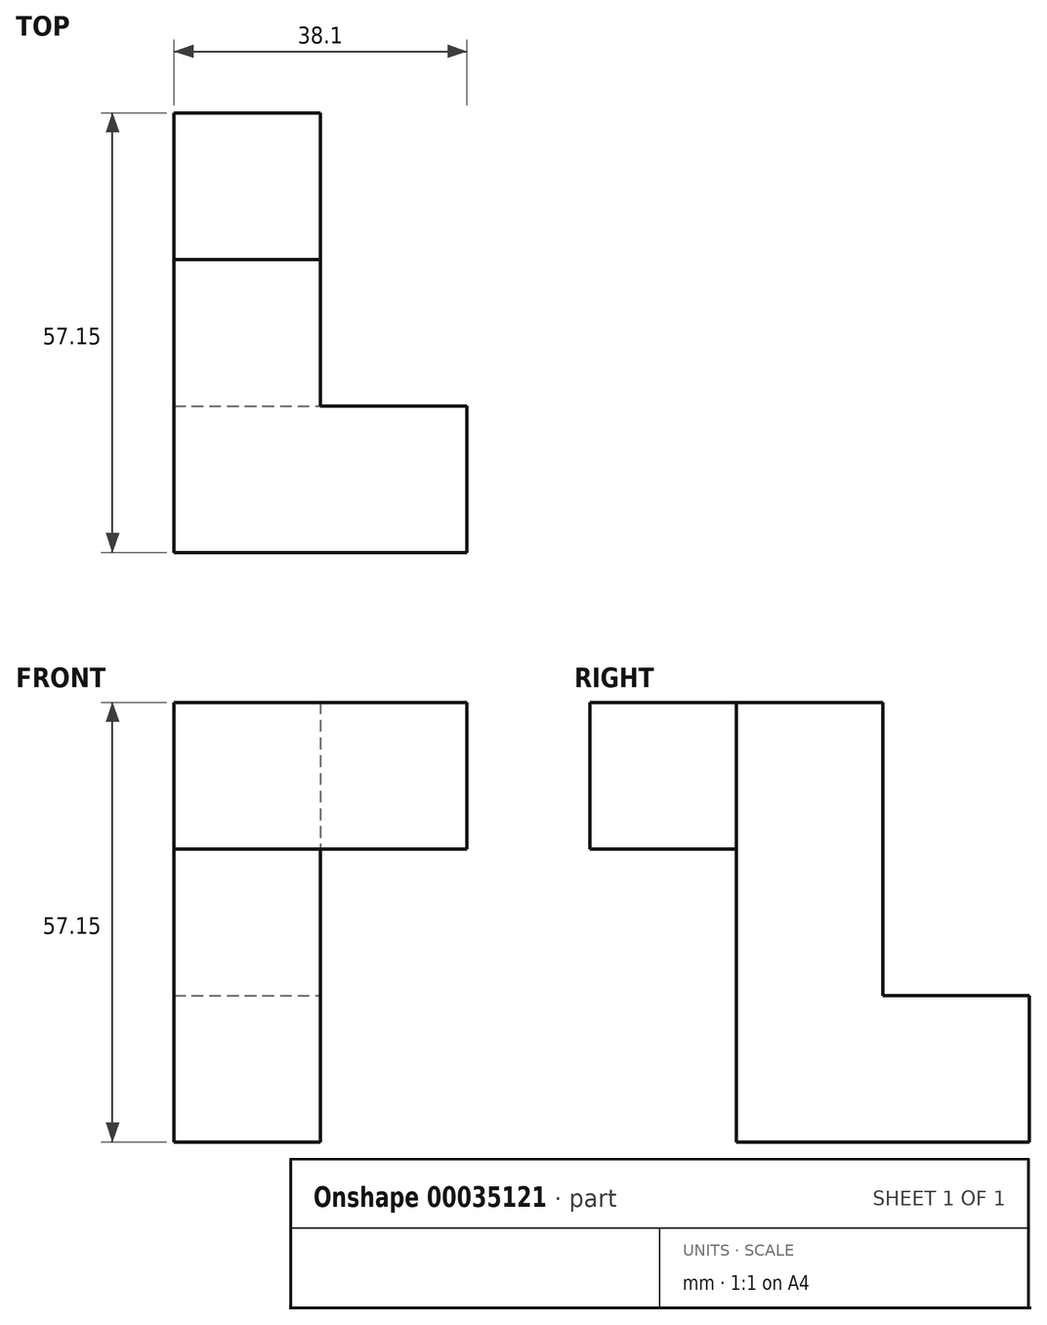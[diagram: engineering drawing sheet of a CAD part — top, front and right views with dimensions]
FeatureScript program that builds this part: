
annotation { "Feature Type Name" : "Feature", "Feature Type Description" : "" }
export const myFeature = defineFeature(function(context is Context, id is Id, definition is map)
    precondition{}
    {
        {
            var Q0;
            Q0=qCreatedBy(makeId("Top.planeOp"),FACE);
            var sketch = newSketch(context, id + "F0", { "sketchPlane" : qUnion([Q0])});
            skLineSegment(sketch, "E0.bottom", {"start": v(0, 0) * mm, "end": v(19.05, 0) * mm});
            skLineSegment(sketch, "E0.top", {"start": v(0, 38.1) * mm, "end": v(19.05, 38.1) * mm});
            skLineSegment(sketch, "E0.left", {"start": v(0, 0) * mm, "end": v(0, 38.1) * mm});
            skLineSegment(sketch, "E0.right", {"start": v(19.05, 0) * mm, "end": v(19.05, 38.1) * mm});
            skSolve(sketch);
        }
        {
            var Q0;
            Q0 = qSketchRegion(id + "F0", true);
            extrude(context, id + "F1", {"entities" : qUnion([Q0]), "depth" : 19.05 * mm});
        }
        {
            var Q0;
            Q0=makeQuery(id+"F1.opExtrude","CAP_FACE",FACE,{"disambiguationData":[OSD([sQuery(id+"F0.wireOp",EDGE,"E0.bottom"),sQuery(id+"F0.wireOp",EDGE,"E0.top"),sQuery(id+"F0.wireOp",EDGE,"E0.left"),sQuery(id+"F0.wireOp",EDGE,"E0.right")])],"isStart":false});
            var sketch = newSketch(context, id + "F2", { "sketchPlane" : qUnion([Q0])});
            skLineSegment(sketch, "E1.bottom", {"start": v(0, 0) * mm, "end": v(19.05, 0) * mm});
            skLineSegment(sketch, "E1.top", {"start": v(0, 19.05) * mm, "end": v(19.05, 19.05) * mm});
            skLineSegment(sketch, "E1.left", {"start": v(0, 0) * mm, "end": v(0, 19.05) * mm});
            skLineSegment(sketch, "E1.right", {"start": v(19.05, 0) * mm, "end": v(19.05, 19.05) * mm});
            skSolve(sketch);
        }
        {
            var Q0;
            Q0 = qSketchRegion(id + "F2", true);
            extrude(context, id + "F3", {"entities" : qUnion([Q0]), "operationType" : NewBodyOperationType.ADD, "depth" : 38.1 * mm});
        }
        {
            var Q0;
            Q0=makeQuery(id+"F3.boolean.opBoolean","MERGE",FACE,{"derivedFrom":[makeQuery(id+"F1.opExtrude","SWEPT_FACE",FACE,{"disambiguationData":[OSD([sQuery(id+"F0.wireOp",EDGE,"E0.bottom")])]}),makeQuery(id+"F3.opExtrude","SWEPT_FACE",FACE,{"disambiguationData":[OSD([sQuery(id+"F2.wireOp",EDGE,"E1.bottom")])]})]});
            var sketch = newSketch(context, id + "F4", { "sketchPlane" : qUnion([Q0])});
            skLineSegment(sketch, "E2.bottom", {"start": v(0, 57.15) * mm, "end": v(19.05, 57.15) * mm});
            skLineSegment(sketch, "E2.top", {"start": v(0, 38.1) * mm, "end": v(19.05, 38.1) * mm});
            skLineSegment(sketch, "E2.left", {"start": v(0, 57.15) * mm, "end": v(0, 38.1) * mm});
            skLineSegment(sketch, "E2.right", {"start": v(19.05, 57.15) * mm, "end": v(19.05, 38.1) * mm});
            skSolve(sketch);
        }
        {
            var Q0;
            Q0=makeQuery(id+"F4.imprint","IMPRINT",FACE,{"disambiguationData":[TD([[makeQuery(id+"F4.imprint","IMPRINT",EDGE,{"derivedFrom":sQuery(id+"F4.wireOp",EDGE,"E2.bottom")}),-1.0]])]});
            extrude(context, id + "F5", {"entities" : qUnion([Q0]), "operationType" : NewBodyOperationType.ADD, "depth" : 19.05 * mm});
        }
        {
            var Q0;
            Q0=makeQuery(id+"F5.boolean.opBoolean","MERGE",FACE,{"derivedFrom":[makeQuery(id+"F3.boolean.opBoolean","MERGE",FACE,{"derivedFrom":[makeQuery(id+"F1.opExtrude","SWEPT_FACE",FACE,{"disambiguationData":[OSD([sQuery(id+"F0.wireOp",EDGE,"E0.right")])]}),makeQuery(id+"F3.opExtrude","SWEPT_FACE",FACE,{"disambiguationData":[OSD([sQuery(id+"F2.wireOp",EDGE,"E1.right")])]})]}),makeQuery(id+"F5.opExtrude","SWEPT_FACE",FACE,{"disambiguationData":[OSD([sQuery(id+"F4.wireOp",EDGE,"E2.right")])]})]});
            var sketch = newSketch(context, id + "F6", { "sketchPlane" : qUnion([Q0])});
            skLineSegment(sketch, "E3.bottom", {"start": v(-19.05, 57.15) * mm, "end": v(0, 57.15) * mm});
            skLineSegment(sketch, "E3.top", {"start": v(-19.05, 38.1) * mm, "end": v(0, 38.1) * mm});
            skLineSegment(sketch, "E3.left", {"start": v(-19.05, 57.15) * mm, "end": v(-19.05, 38.1) * mm});
            skLineSegment(sketch, "E3.right", {"start": v(0, 57.15) * mm, "end": v(0, 38.1) * mm});
            skSolve(sketch);
        }
        {
            var Q0;
            Q0=makeQuery(id+"F6.imprint","IMPRINT",FACE,{"disambiguationData":[TD([[makeQuery(id+"F6.imprint","IMPRINT",EDGE,{"derivedFrom":sQuery(id+"F6.wireOp",EDGE,"E3.bottom")}),-1.0]])]});
            extrude(context, id + "F7", {"entities" : qUnion([Q0]), "operationType" : NewBodyOperationType.ADD, "depth" : 19.05 * mm});
        }
    });
